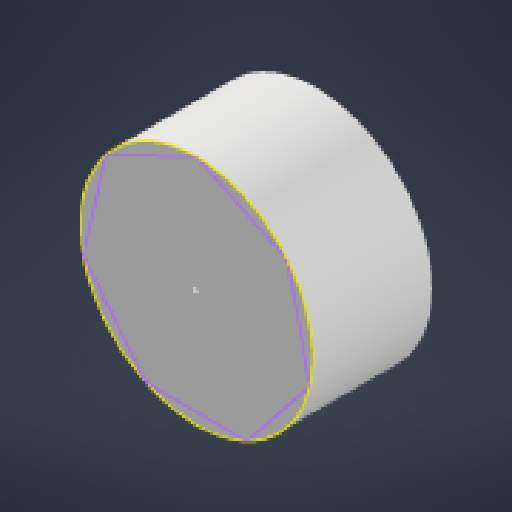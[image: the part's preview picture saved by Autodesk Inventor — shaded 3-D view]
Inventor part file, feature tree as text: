
AUTODESK INVENTOR PART (.ipt)
format: ipt  version: 2024 (Build 280153000, 153)  size: 1,056,256 bytes
history: native  units: mm
features: sketch x20, other x12, loft x7, extrude x6, fillet x1, revolve x1, projected_geometry x1
ambient origin geometry x8: Origin, YZ Plane, XZ Plane, XY Plane, X Axis, Y Axis, Z Axis, Center Point
bodies: Body1 (feature_tree), Body2 (feature_tree), Body3 (feature_tree)
feature tree (48):
  other  "솔리드1"
  extrude  "돌출1"  Depth=20.0mm
  extrude  "돌출2"  Depth=35.0mm
  sketch  "스케치3"
  extrude  "돌출3"  Depth=18.0mm TaperAngle=0.0deg
  loft  "로프트1"
  loft  "로프트3"
  loft  "로프트4"
  loft  "로프트5"
  loft  "로프트6"
  loft  "로프트7"
  loft  "로프트8"
  extrude  "돌출4"  TaperAngle=0.0deg  [1 undecoded]
  fillet  "모깎기1"  [1 undecoded]
  other  "직접 편집1"
  other  "직접 편집2"
  extrude  "돌출5"  Depth=35.0mm
  revolve  "회전1"
  extrude  "돌출6"  Depth=1.0mm
  sketch  "스케치1"
  sketch  "스케치2"
  projected_geometry  "투영된 루프1"
  sketch  "스케치5"
  sketch  "스케치6"
  other  "솔리드2"
  sketch  "스케치20"
  sketch  "스케치21"
  sketch  "스케치22"
  sketch  "스케치23"
  sketch  "스케치24"
  sketch  "스케치25"
  sketch  "스케치26"
  sketch  "스케치27"
  sketch  "스케치28"
  sketch  "스케치29"
  sketch  "스케치30"
  sketch  "스케치31"
  sketch  "스케치33"
  sketch  "스케치34"
  sketch  "스케치35"
  other  "이동1"
  other  "이동2"
  other  "이동3"
  other  "이동4"
  other  "이동5"
  other  "이동6"
  other  "이동7"
  other  "이동8"
note: 2 required parameter values undecoded (feature->parameter linkage not recoverable at this tier; creation-order binding heuristic only, values carry confidence <= 0.55)
